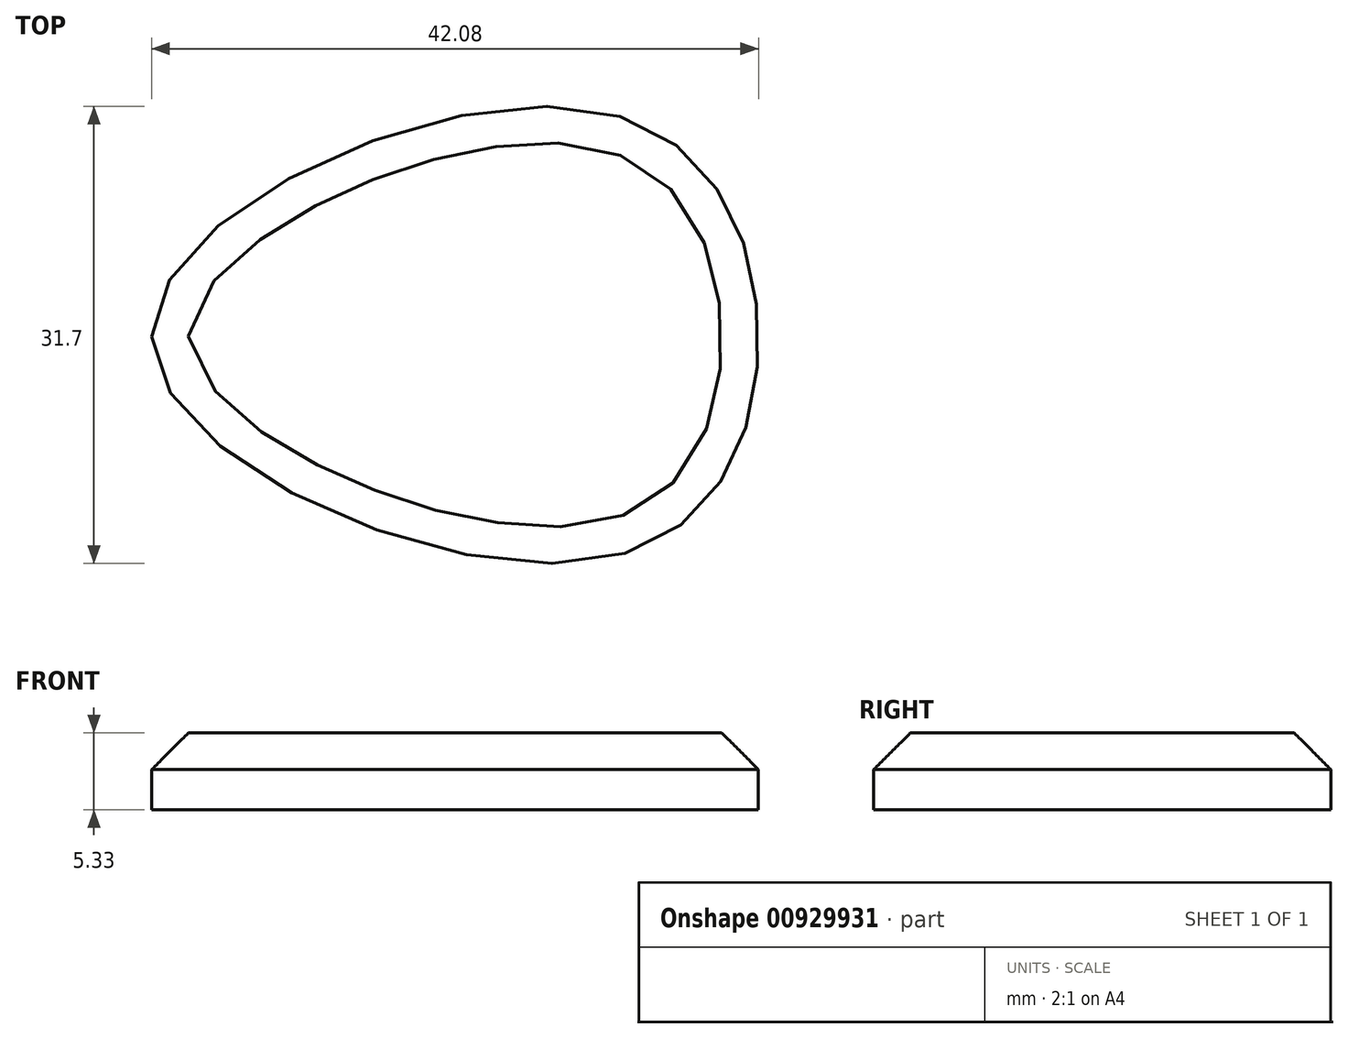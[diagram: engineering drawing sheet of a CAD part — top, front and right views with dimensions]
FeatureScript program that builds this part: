
annotation { "Feature Type Name" : "Feature", "Feature Type Description" : "" }
export const myFeature = defineFeature(function(context is Context, id is Id, definition is map)
    precondition{}
    {
        {
            var Q0;
            Q0=qCreatedBy(makeId("Top.planeOp"),FACE);
            var sketch = newSketch(context, id + "F0", { "sketchPlane" : qUnion([Q0])});
            skFitSpline(sketch, "E0", {"points": [v(0, 0) * mm, v(30.86, -15.5) * mm, v(42.08, 0) * mm, v(30.32, 15.76) * mm, v(0, 0) * mm]});
            skSolve(sketch);
        }
        {
            var Q0;
            Q0=makeQuery(id+"F0.imprint","IMPRINT",FACE,{"disambiguationData":[TD([[makeQuery(id+"F0.imprint","IMPRINT",EDGE,{"derivedFrom":sQuery(id+"F0.wireOp",EDGE,"E0")}),1.0]])]});
            extrude(context, id + "F1", {"entities" : qUnion([Q0]), "depth" : 5.33 * mm, "offsetDistance" : 25.4 * mm});
        }
        {
            var Q0;
            Q0=makeQuery(id+"F1.opExtrude","CAP_EDGE",EDGE,{"disambiguationData":[OSD([sQuery(id+"F0.wireOp",EDGE,"E0")])],"isStart":false});
            chamfer(context, id + "F2", {"entities" : qUnion([Q0]), "width" : 2.54 * mm, "tangentPropagation" : true});
        }
    });
